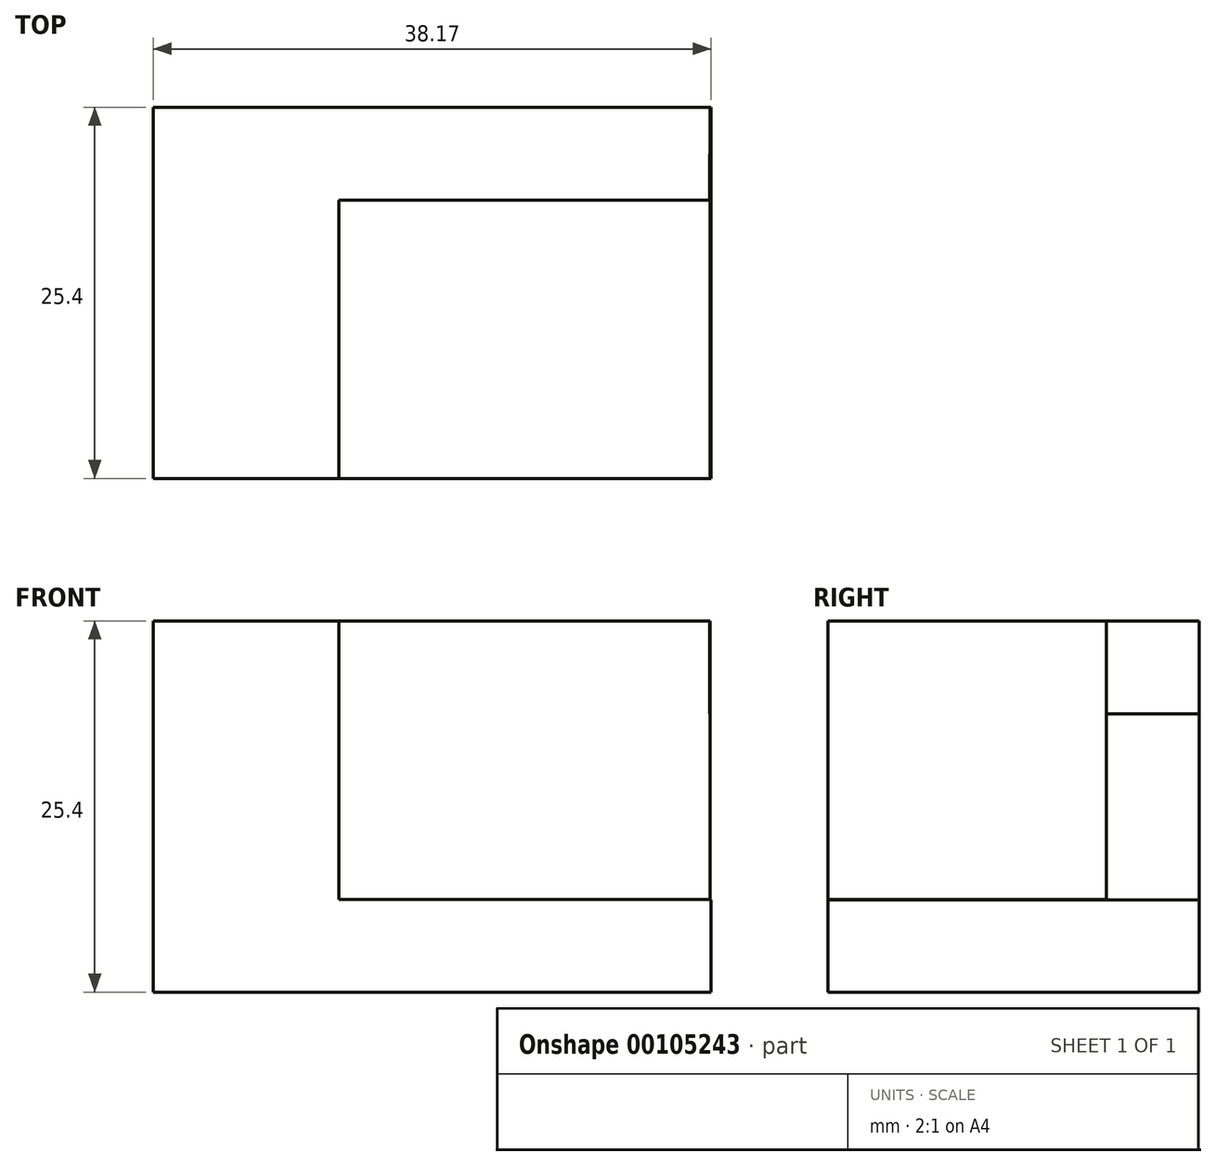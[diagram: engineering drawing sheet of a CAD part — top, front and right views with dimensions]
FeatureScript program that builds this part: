
annotation { "Feature Type Name" : "Feature", "Feature Type Description" : "" }
export const myFeature = defineFeature(function(context is Context, id is Id, definition is map)
    precondition{}
    {
        {
            var Q0;
            Q0=qCreatedBy(makeId("Front.planeOp"),FACE);
            var sketch = newSketch(context, id + "F0", { "sketchPlane" : qUnion([Q0])});
            skLineSegment(sketch, "E0", {"start": v(0, 0) * mm, "end": v(0, 25.4) * mm});
            skLineSegment(sketch, "E1", {"start": v(0, 0) * mm, "end": v(38.17, 0) * mm});
            skLineSegment(sketch, "E2", {"start": v(38.17, 0) * mm, "end": v(38.17, 19.05) * mm});
            skLineSegment(sketch, "E3", {"start": v(38.17, 19.05) * mm, "end": v(12.7, 19.05) * mm});
            skLineSegment(sketch, "E4", {"start": v(12.7, 19.05) * mm, "end": v(12.7, 25.4) * mm});
            skLineSegment(sketch, "E5", {"start": v(12.7, 25.4) * mm, "end": v(0, 25.4) * mm});
            skLineSegment(sketch, "E6", {"start": v(12.7, 19.05) * mm, "end": v(12.7, 6.31) * mm});
            skLineSegment(sketch, "E7", {"start": v(12.7, 6.31) * mm, "end": v(38.17, 6.31) * mm});
            skLineSegment(sketch, "E8", {"start": v(38.17, 6.31) * mm, "end": v(38.17, 19.05) * mm});
            skSolve(sketch);
        }
        {
            var Q0;
            Q0=qCreatedBy(makeId("Right.planeOp"),FACE);
            var sketch = newSketch(context, id + "F1", { "sketchPlane" : qUnion([Q0])});
            skLineSegment(sketch, "E9", {"start": v(0, 0) * mm, "end": v(25.4, 0) * mm});
            skLineSegment(sketch, "E10", {"start": v(25.4, 0) * mm, "end": v(25.4, 19.05) * mm});
            skLineSegment(sketch, "E11", {"start": v(25.4, 19.05) * mm, "end": v(19.05, 19.05) * mm});
            skLineSegment(sketch, "E12", {"start": v(19.05, 19.05) * mm, "end": v(19.05, 6.35) * mm});
            skLineSegment(sketch, "E13", {"start": v(19.05, 6.35) * mm, "end": v(0, 6.35) * mm});
            skLineSegment(sketch, "E14", {"start": v(0, 6.35) * mm, "end": v(0, 0) * mm});
            skLineSegment(sketch, "E15", {"start": v(25.4, 19.05) * mm, "end": v(25.4, 25.4) * mm});
            skLineSegment(sketch, "E16", {"start": v(25.4, 25.4) * mm, "end": v(0, 25.4) * mm});
            skLineSegment(sketch, "E17", {"start": v(0, 25.4) * mm, "end": v(0, 6.35) * mm});
            skSolve(sketch);
        }
        {
            var Q0;
            Q0=qCreatedBy(makeId("Top.planeOp"),FACE);
            var sketch = newSketch(context, id + "F2", { "sketchPlane" : qUnion([Q0])});
            skLineSegment(sketch, "E18", {"start": v(0, 0) * mm, "end": v(0, 25.4) * mm});
            skLineSegment(sketch, "E19", {"start": v(0, 25.4) * mm, "end": v(38.1, 25.4) * mm});
            skLineSegment(sketch, "E20", {"start": v(0, 0) * mm, "end": v(12.67, 0) * mm});
            skLineSegment(sketch, "E21", {"start": v(12.67, 0) * mm, "end": v(12.67, 19.05) * mm});
            skLineSegment(sketch, "E22", {"start": v(12.67, 19.05) * mm, "end": v(38.07, 19.05) * mm});
            skLineSegment(sketch, "E23", {"start": v(38.07, 19.05) * mm, "end": v(38.1, 25.4) * mm});
            skLineSegment(sketch, "E24", {"start": v(38.07, 19.05) * mm, "end": v(38.07, 0) * mm});
            skLineSegment(sketch, "E25", {"start": v(38.07, 0) * mm, "end": v(0, 0) * mm});
            skSolve(sketch);
        }
        {
            var Q0;
            Q0=makeQuery(id+"F0.imprint","IMPRINT",FACE,{"disambiguationData":[TD([[makeQuery(id+"F0.imprint","IMPRINT",EDGE,{"derivedFrom":sQuery(id+"F0.wireOp",EDGE,"E0")}),-1.0]])]});
            extrude(context, id + "F3", {"entities" : qUnion([Q0]), "oppositeDirection" : true, "depth" : 25.4 * mm});
        }
        {
            var Q0;
            Q0=makeQuery(id+"F1.imprint","IMPRINT",FACE,{"disambiguationData":[TD([[makeQuery(id+"F1.imprint","IMPRINT",EDGE,{"derivedFrom":sQuery(id+"F1.wireOp",EDGE,"E9")}),1.0]])]});
            extrude(context, id + "F4", {"entities" : qUnion([Q0]), "operationType" : NewBodyOperationType.ADD, "depth" : 38.1 * mm});
        }
        {
            var Q0;
            {var subQ1=sQuery(id+"F2.wireOp",EDGE,"E18");Q0=makeQuery(id+"F2.imprint","IMPRINT",FACE,{"disambiguationData":[TD([[makeQuery(id+"F2.imprint","IMPRINT",EDGE,{"derivedFrom":subQ1}),-1.0]])]});}
            extrude(context, id + "F5", {"entities" : qUnion([Q0]), "operationType" : NewBodyOperationType.ADD, "depth" : 25.4 * mm});
        }
    });
